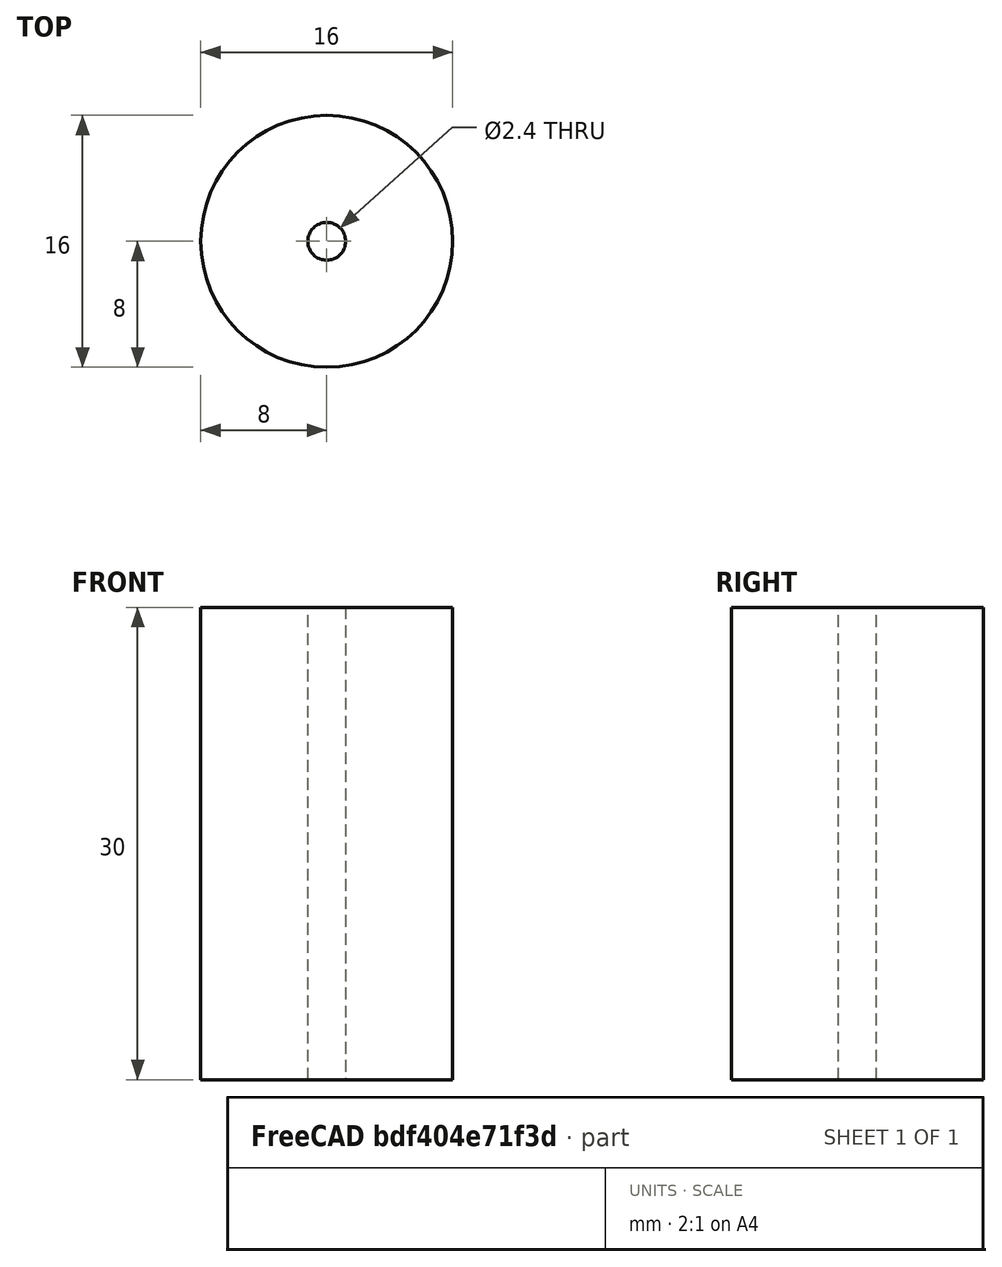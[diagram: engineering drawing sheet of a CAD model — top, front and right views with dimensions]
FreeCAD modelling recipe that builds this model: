
FCSTD DOCUMENT  (FreeCAD 0.21R33668 +26 (Git))
Label: board_connector
License: All rights reserved
LicenseURL: https://en.wikipedia.org/wiki/All_rights_reserved
objects: Sketcher::SketchObject×2, PartDesign::Pad×1, PartDesign::Pocket×1, PartDesign::Body×1
note: 7 computed .brp shape members not serialized (recipe doc carries the construction recipe); baked Part::Feature solids carry a one-line shape summary decoded from their .brp

FEATURE [Sketcher::SketchObject] Sketch
  FullyConstrained = false
  MapMode = 5
  Support = -> [XY_Plane]
  sketch-geometry (2):
    g0: Circle CenterX=0 CenterY=0 CenterZ=0 NormalX=0 NormalY=0 NormalZ=1 AngleXU=0 Radius=8
    g1: GeomPoint X=-5.04833 Y=6.206 Z=0
  constraints (3):
    c: Coincident(g0,g-1)
    c: PointOnObject(g1,g0)
    c: Distance(g1,g0) = 8
FEATURE [PartDesign::Pad] Pad
  Direction = (0,0,1)
  Length = 30
  Length2 = 10
  Profile = -> Sketch
  ReferenceAxis = -> Sketch [N_Axis]
  Type = 0
FEATURE [Sketcher::SketchObject] Sketch001
  FullyConstrained = false
  MapMode = 5
  Placement = pos=(0,0,30) rot=(0,0,1;0rad)
  Support = -> [Pad]
  sketch-geometry (2):
    g0: Circle CenterX=0 CenterY=0 CenterZ=0 NormalX=0 NormalY=0 NormalZ=1 AngleXU=0 Radius=1.2
    g1: GeomPoint X=-0.940143 Y=0.745742 Z=0
  constraints (3):
    c: Coincident(g0,g-1)
    c: PointOnObject(g1,g0)
    c: Distance(g1,g0) = 1.2
FEATURE [PartDesign::Pocket] Pocket
  BaseFeature = -> Pad
  Direction = (0,0,-1)
  Length = 35
  Length2 = 5
  Profile = -> Sketch001
  ReferenceAxis = -> Sketch001 [N_Axis]
  Type = 0
FEATURE [PartDesign::Body] Body
  Group = -> [Sketch,Pad,Sketch001,Pocket]
  Origin = -> Origin
  Tip = -> Pocket
